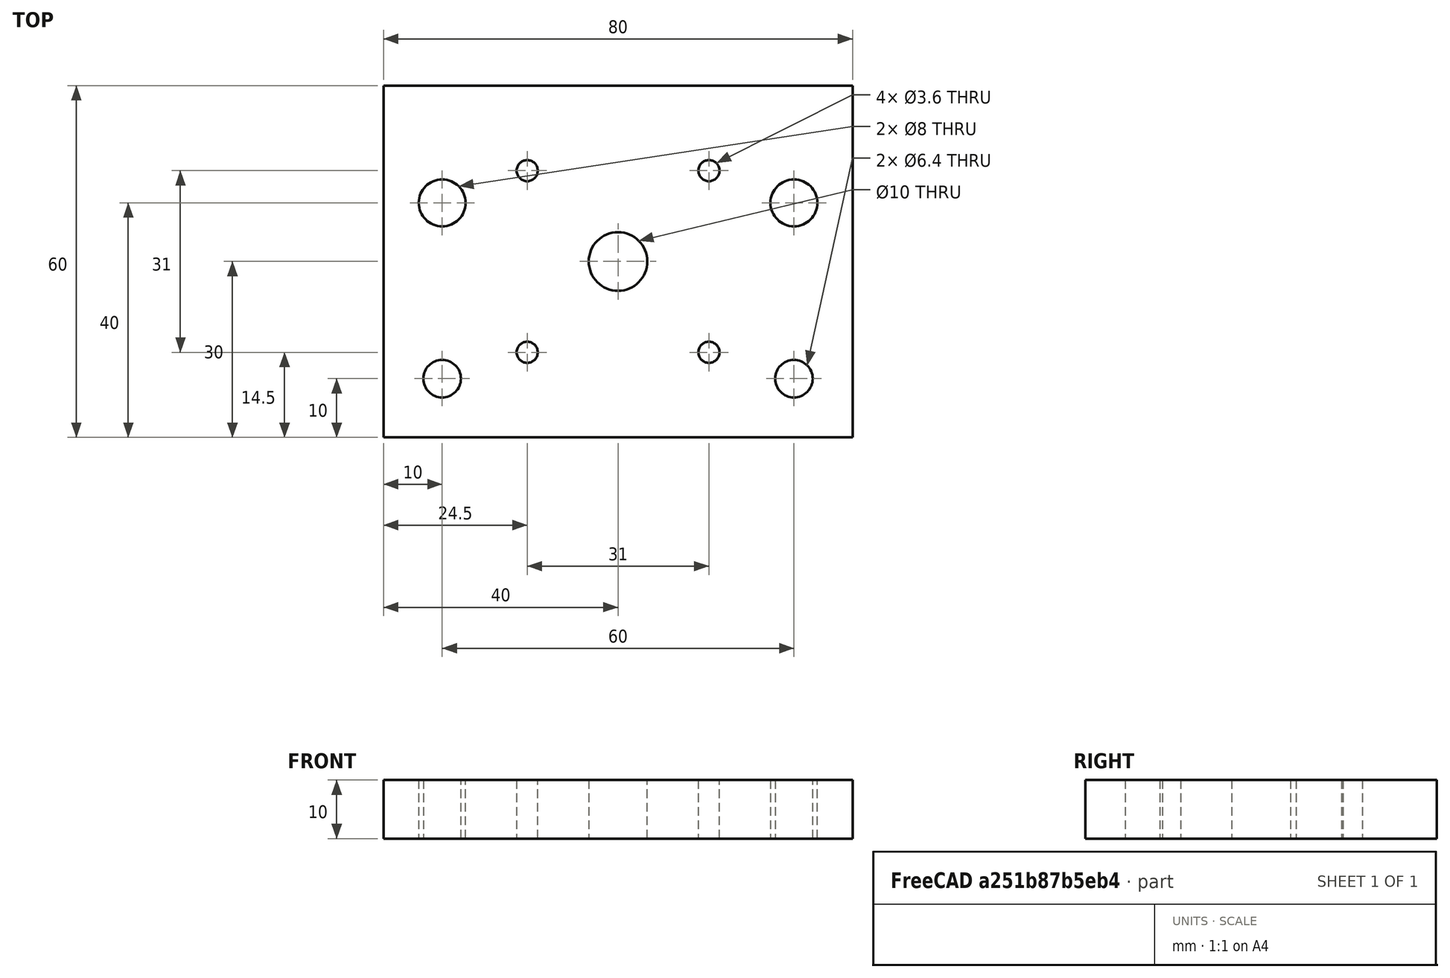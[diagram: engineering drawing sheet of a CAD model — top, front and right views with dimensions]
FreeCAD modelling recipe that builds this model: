
FCSTD DOCUMENT  (FreeCAD 0.18R16110 (Git))
Label: mountplate
License: All rights reserved
LicenseURL: http://en.wikipedia.org/wiki/All_rights_reserved
objects: Sketcher::SketchObject×1, PartDesign::Pad×1, PartDesign::Body×1
note: 4 computed .brp shape members not serialized (recipe doc carries the construction recipe); baked Part::Feature solids carry a one-line shape summary decoded from their .brp

FEATURE [Sketcher::SketchObject] Sketch
  MapMode = 5
  Support = -> [XY_Plane]
  sketch-geometry (13):
    g0: LineSegment StartX=0 StartY=60 StartZ=0 EndX=80 EndY=60 EndZ=0
    g1: LineSegment StartX=80 StartY=60 StartZ=0 EndX=80 EndY=0 EndZ=0
    g2: LineSegment StartX=80 StartY=0 StartZ=0 EndX=0 EndY=0 EndZ=0
    g3: LineSegment StartX=0 StartY=0 StartZ=0 EndX=0 EndY=60 EndZ=0
    g4: Circle CenterX=40 CenterY=30 CenterZ=0 NormalX=0 NormalY=0 NormalZ=1 AngleXU=0 Radius=5
    g5: Circle CenterX=55.5 CenterY=45.5 CenterZ=0 NormalX=0 NormalY=0 NormalZ=1 AngleXU=0 Radius=1.8
    g6: Circle CenterX=55.5 CenterY=14.5 CenterZ=0 NormalX=0 NormalY=0 NormalZ=1 AngleXU=0 Radius=1.8
    g7: Circle CenterX=24.5 CenterY=14.5 CenterZ=0 NormalX=0 NormalY=0 NormalZ=1 AngleXU=0 Radius=1.8
    g8: Circle CenterX=24.5 CenterY=45.5 CenterZ=0 NormalX=0 NormalY=0 NormalZ=1 AngleXU=0 Radius=1.8
    g9: Circle CenterX=10 CenterY=10 CenterZ=0 NormalX=0 NormalY=0 NormalZ=1 AngleXU=0 Radius=3.2
    g10: Circle CenterX=70 CenterY=10 CenterZ=0 NormalX=0 NormalY=0 NormalZ=1 AngleXU=0 Radius=3.2
    g11: Circle CenterX=70 CenterY=40 CenterZ=0 NormalX=0 NormalY=0 NormalZ=1 AngleXU=0 Radius=4
    g12: Circle CenterX=10 CenterY=40 CenterZ=0 NormalX=0 NormalY=0 NormalZ=1 AngleXU=0 Radius=4
  constraints (38):
    c: Coincident(g0,g1)
    c: Coincident(g1,g2)
    c: Coincident(g2,g3)
    c: Coincident(g3,g0)
    c: Horizontal(g0)
    c: Horizontal(g2)
    c: Vertical(g1)
    c: Vertical(g3)
    c: Coincident(g2,g-1)
    c: DistanceY(g3,g3) = 60
    c: DistanceX(g2,g2) = 80
    c: DistanceX(g2,g4) = 40
    c: DistanceY(g2,g4) = 30
    c: Radius(g4) = 5
    c: DistanceY(g4,g5) = 15.5
    c: DistanceX(g6,g5) = 0
    c: DistanceX(g4,g5) = 15.5
    c: DistanceY(g8,g5) = 0
    c: DistanceX(g8,g5) = 31
    c: DistanceX(g7,g8) = 0
    c: DistanceY(g6,g5) = 31
    c: DistanceY(g6,g7) = 0
    c: Radius(g8) = 1.8
    c: Equal(g8,g5)
    c: Equal(g8,g6)
    c: Equal(g8,g7)
    c: DistanceX(g2,g9) = 10
    c: DistanceY(g2,g9) = 10
    c: DistanceY(g9,g10) = 0
    c: DistanceX(g10,g1) = 10
    c: DistanceX(g12,g9) = 0
    c: DistanceY(g11,g12) = 0
    c: DistanceX(g11,g0) = 10
    c: DistanceY(g12,g0) = 20
    c: Radius(g9) = 3.2
    c: Equal(g9,g10)
    c: Radius(g12) = 4
    c: Equal(g12,g11)
FEATURE [PartDesign::Pad] Pad
  Length = 10
  Length2 = 100
  Profile = -> Sketch
  Type = 0
FEATURE [PartDesign::Body] Body
  Group = -> [Sketch,Pad]
  Origin = -> Origin
  Tip = -> Pad
